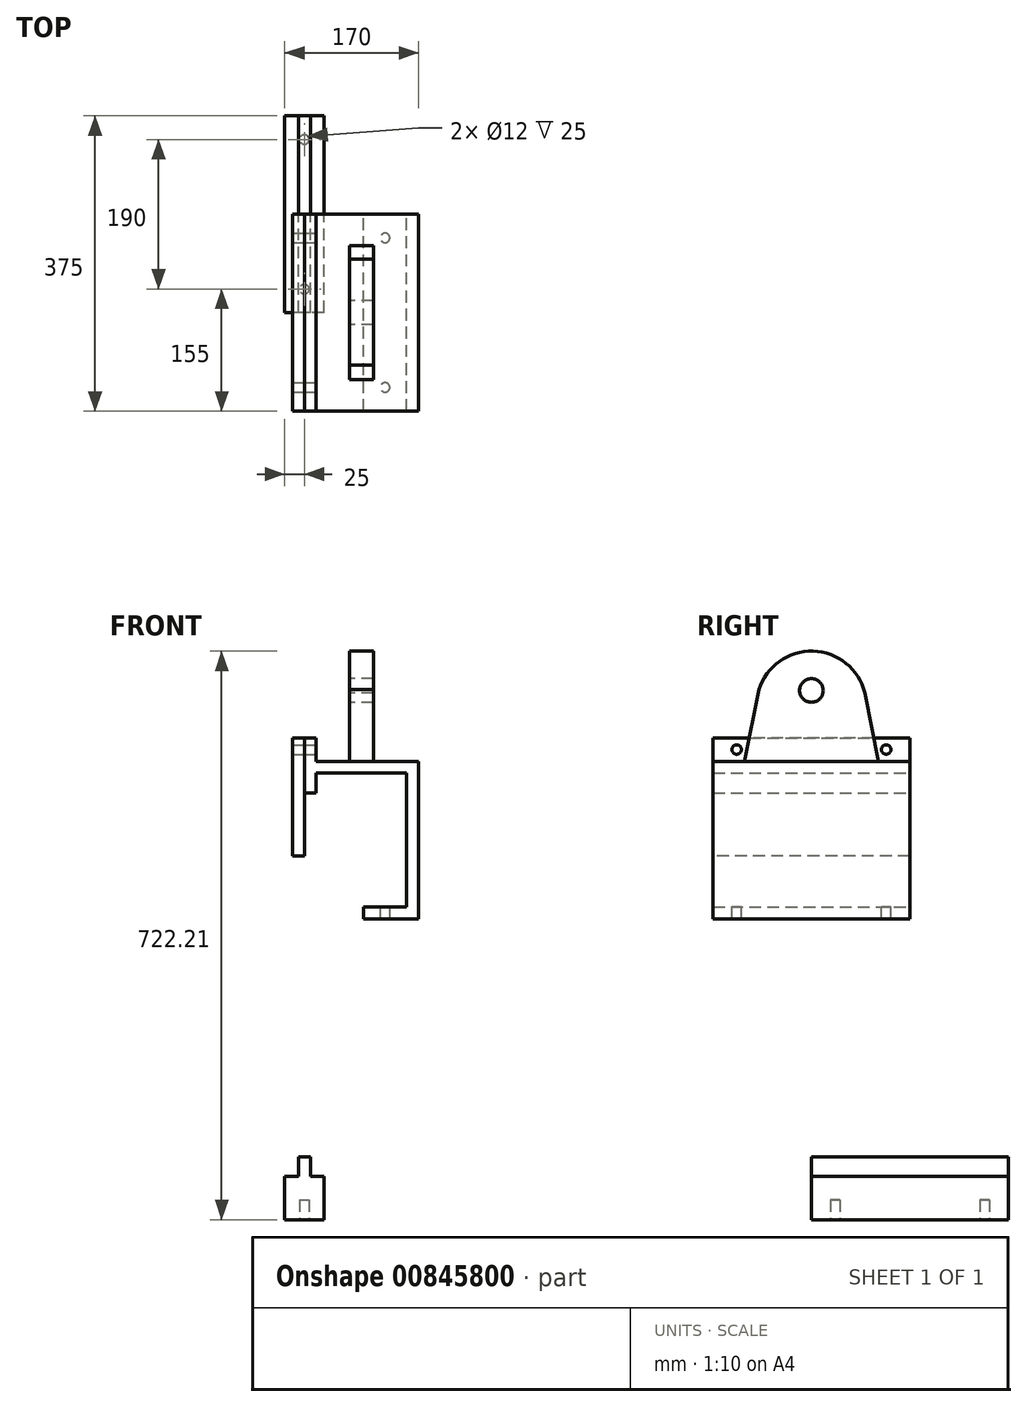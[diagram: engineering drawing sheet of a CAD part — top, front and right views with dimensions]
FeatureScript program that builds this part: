
annotation { "Feature Type Name" : "Feature", "Feature Type Description" : "" }
export const myFeature = defineFeature(function(context is Context, id is Id, definition is map)
    precondition{}
    {
        {
            var Q0;
            Q0=qCreatedBy(makeId("Front.planeOp"),FACE);
            var sketch = newSketch(context, id + "F0", { "sketchPlane" : qUnion([Q0])});
            skLineSegment(sketch, "E0", {"start": v(42.62, 18.6) * mm, "end": v(42.62, -96.4) * mm});
            skLineSegment(sketch, "E1", {"start": v(42.62, -96.4) * mm, "end": v(22.55, -96.4) * mm});
            skLineSegment(sketch, "E2", {"start": v(22.55, -96.4) * mm, "end": v(22.55, -88.4) * mm});
            skLineSegment(sketch, "E3", {"start": v(22.55, -88.4) * mm, "end": v(32.62, -88.4) * mm});
            skLineSegment(sketch, "E4", {"start": v(32.62, -88.4) * mm, "end": v(32.62, -31.1) * mm});
            skLineSegment(sketch, "E5", {"start": v(32.62, -31.1) * mm, "end": v(-23.38, -31.1) * mm});
            skLineSegment(sketch, "E6", {"start": v(-23.38, -31.1) * mm, "end": v(-23.38, -88.4) * mm});
            skLineSegment(sketch, "E7", {"start": v(-23.38, -88.4) * mm, "end": v(-4.88, -88.4) * mm});
            skLineSegment(sketch, "E8", {"start": v(-4.88, -88.4) * mm, "end": v(-4.88, -96.4) * mm});
            skLineSegment(sketch, "E9", {"start": v(-4.88, -96.4) * mm, "end": v(-30.88, -96.4) * mm});
            skLineSegment(sketch, "E10", {"start": v(-30.88, -96.4) * mm, "end": v(-30.88, -132.4) * mm});
            skLineSegment(sketch, "E11", {"start": v(-30.88, -132.4) * mm, "end": v(-34.88, -132.4) * mm});
            skLineSegment(sketch, "E12", {"start": v(-34.88, -132.4) * mm, "end": v(-34.88, -99.6) * mm});
            skLineSegment(sketch, "E13", {"start": v(-34.88, -99.6) * mm, "end": v(-65.38, -99.6) * mm});
            skLineSegment(sketch, "E14", {"start": v(-65.38, -99.6) * mm, "end": v(-65.38, -132.4) * mm});
            skLineSegment(sketch, "E15", {"start": v(-65.38, -132.4) * mm, "end": v(-70.38, -132.4) * mm});
            skLineSegment(sketch, "E16", {"start": v(-70.38, -132.4) * mm, "end": v(-70.38, 18.6) * mm});
            skPoint(sketch, "E17.end.orphan", {"position": v(-38.43, 18.6) * mm});
            skLineSegment(sketch, "E18", {"start": v(-70.38, 18.6) * mm, "end": v(42.62, 18.6) * mm});
            skLineSegment(sketch, "E19", {"start": v(0, 0) * mm, "end": v(242.06, 0) * mm});
            skLineSegment(sketch, "E20", {"start": v(242.06, -153.05) * mm, "end": v(242.06, 16.95) * mm});
            skLineSegment(sketch, "E21", {"start": v(242.06, 16.95) * mm, "end": v(342.06, 16.95) * mm});
            skLineSegment(sketch, "E22", {"start": v(342.06, 16.95) * mm, "end": v(342.06, -153.05) * mm});
            skLineSegment(sketch, "E23", {"start": v(342.06, -153.05) * mm, "end": v(242.06, -153.05) * mm});
            skLineSegment(sketch, "E24", {"start": v(75, 397.21) * mm, "end": v(130, 397.21) * mm});
            skLineSegment(sketch, "E25", {"start": v(130, 397.21) * mm, "end": v(130, 567.21) * mm});
            skLineSegment(sketch, "E26", {"start": v(130, 567.21) * mm, "end": v(15, 567.21) * mm});
            skLineSegment(sketch, "E27", {"start": v(15, 567.21) * mm, "end": v(15, 542.21) * mm});
            skLineSegment(sketch, "E28", {"start": v(75, 397.21) * mm, "end": v(75, 382.21) * mm});
            skLineSegment(sketch, "E29", {"start": v(75, 382.21) * mm, "end": v(145, 382.21) * mm});
            skLineSegment(sketch, "E30", {"start": v(145, 382.21) * mm, "end": v(145, 582.21) * mm});
            skLineSegment(sketch, "E31", {"start": v(145, 582.21) * mm, "end": v(0, 582.21) * mm});
            skLineSegment(sketch, "E32", {"start": v(0, 582.21) * mm, "end": v(0, 542.21) * mm});
            skLineSegment(sketch, "E33", {"start": v(0, 542.21) * mm, "end": v(15, 542.21) * mm});
            skSolve(sketch);
        }
        {
            var Q0;
            Q0=makeQuery(id+"F0.imprint","IMPRINT",FACE,{"disambiguationData":[TD([[makeQuery(id+"F0.imprint","IMPRINT",EDGE,{"derivedFrom":sQuery(id+"F0.wireOp",EDGE,"E24")}),-1.0]])]});
            extrude(context, id + "F1", {"entities" : qUnion([Q0]), "depth" : 250 * mm, "offsetDistance" : 25 * mm});
        }
        {
            var Q0;
            Q0=makeQuery(id+"F1.opExtrude","SWEPT_FACE",FACE,{"disambiguationData":[OSD([sQuery(id+"F0.wireOp",EDGE,"E24")])]});
            var sketch = newSketch(context, id + "F2", { "sketchPlane" : qUnion([Q0])});
            skCircle(sketch, "E34", {"center": v(102.5, -220) * mm, "radius": 6 * mm});
            skPoint(sketch, "E34.centerSnap0", {"position": v(102.5, -250) * mm});
            skCircle(sketch, "E35", {"center": v(102.5, -30) * mm, "radius": 6 * mm});
            skPoint(sketch, "E35.centerSnap0", {"position": v(102.5, 0) * mm});
            skLineSegment(sketch, "E36", {"start": v(102.5, 0) * mm, "end": v(102.5, -30) * mm});
            skLineSegment(sketch, "E37", {"start": v(102.5, -220) * mm, "end": v(102.5, -250) * mm});
            skSolve(sketch);
        }
        {
            var Q0;
            Q0 = qSketchRegion(id + "F2", true);
            extrude(context, id + "F3", {"entities" : qUnion([Q0]), "operationType" : NewBodyOperationType.REMOVE, "oppositeDirection" : true, "depth" : 15 * mm, "offsetDistance" : 25 * mm});
        }
        {
            var Q0;
            Q0=qCreatedBy(makeId("Top.planeOp"),FACE);
            var sketch = newSketch(context, id + "F4", { "sketchPlane" : qUnion([Q0])});
            skLineSegment(sketch, "E38.bottom", {"start": v(25, -125) * mm, "end": v(-25, -125) * mm});
            skLineSegment(sketch, "E38.top", {"start": v(25, 125) * mm, "end": v(-25, 125) * mm});
            skLineSegment(sketch, "E38.left", {"start": v(25, -125) * mm, "end": v(25, 125) * mm});
            skLineSegment(sketch, "E38.right", {"start": v(-25, -125) * mm, "end": v(-25, 125) * mm});
            skPoint(sketch, "E38.middle", {"position": v(0, 0) * mm});
            skSolve(sketch);
        }
        {
            var Q0;
            Q0 = qSketchRegion(id + "F4", true);
            extrude(context, id + "F5", {"entities" : qUnion([Q0]), "depth" : 55 * mm, "offsetDistance" : 25 * mm});
        }
        {
            var Q0;
            Q0=makeQuery(id+"F5.opExtrude","CAP_FACE",FACE,{"disambiguationData":[OSD([sQuery(id+"F4.wireOp",EDGE,"E38.bottom"),sQuery(id+"F4.wireOp",EDGE,"E38.top"),sQuery(id+"F4.wireOp",EDGE,"E38.left"),sQuery(id+"F4.wireOp",EDGE,"E38.right")])],"isStart":false});
            var sketch = newSketch(context, id + "F6", { "sketchPlane" : qUnion([Q0])});
            skLineSegment(sketch, "E39.bottom", {"start": v(7.5, -125) * mm, "end": v(-7.5, -125) * mm});
            skLineSegment(sketch, "E39.top", {"start": v(7.5, 125) * mm, "end": v(-7.5, 125) * mm});
            skLineSegment(sketch, "E39.left", {"start": v(7.5, -125) * mm, "end": v(7.5, 125) * mm});
            skLineSegment(sketch, "E39.right", {"start": v(-7.5, -125) * mm, "end": v(-7.5, 125) * mm});
            skPoint(sketch, "E39.middle", {"position": v(0, 0) * mm});
            skSolve(sketch);
        }
        {
            var Q0;
            Q0 = qSketchRegion(id + "F6", true);
            extrude(context, id + "F7", {"entities" : qUnion([Q0]), "operationType" : NewBodyOperationType.ADD, "depth" : 25 * mm, "offsetDistance" : 25 * mm});
        }
        {
            var Q0;
            Q0=makeQuery(id+"F5.opExtrude","CAP_FACE",FACE,{"disambiguationData":[OSD([sQuery(id+"F4.wireOp",EDGE,"E38.bottom"),sQuery(id+"F4.wireOp",EDGE,"E38.top"),sQuery(id+"F4.wireOp",EDGE,"E38.left"),sQuery(id+"F4.wireOp",EDGE,"E38.right")])],"isStart":true});
            var sketch = newSketch(context, id + "F8", { "sketchPlane" : qUnion([Q0])});
            skLineSegment(sketch, "E40", {"start": v(0, 125) * mm, "end": v(0, 95) * mm});
            skLineSegment(sketch, "E41", {"start": v(0, -125) * mm, "end": v(0, -95) * mm});
            skCircle(sketch, "E42", {"center": v(0, 95) * mm, "radius": 6 * mm});
            skCircle(sketch, "E43", {"center": v(0, -95) * mm, "radius": 6 * mm});
            skSolve(sketch);
        }
        {
            var Q0;
            Q0 = qSketchRegion(id + "F8", true);
            extrude(context, id + "F9", {"entities" : qUnion([Q0]), "operationType" : NewBodyOperationType.REMOVE, "oppositeDirection" : true, "depth" : 25 * mm, "offsetDistance" : 25 * mm});
        }
        {
            var Q0;
            Q0=makeQuery(id+"F1.opExtrude","SWEPT_FACE",FACE,{"disambiguationData":[OSD([sQuery(id+"F0.wireOp",EDGE,"E31")])]});
            var sketch = newSketch(context, id + "F10", { "sketchPlane" : qUnion([Q0])});
            skLineSegment(sketch, "E44.bottom", {"start": v(87.5, -210) * mm, "end": v(57.5, -210) * mm});
            skLineSegment(sketch, "E44.top", {"start": v(87.5, -40) * mm, "end": v(57.5, -40) * mm});
            skLineSegment(sketch, "E44.left", {"start": v(87.5, -210) * mm, "end": v(87.5, -40) * mm});
            skLineSegment(sketch, "E44.right", {"start": v(57.5, -210) * mm, "end": v(57.5, -40) * mm});
            skPoint(sketch, "E44.middle", {"position": v(72.5, -125) * mm});
            skPoint(sketch, "E44.middle.positionSnap0", {"position": v(72.5, 0) * mm});
            skPoint(sketch, "E44.middle.positionSnap1", {"position": v(0, -125) * mm});
            skPoint(sketch, "E44.centerSnap0", {"position": v(72.5, 0) * mm});
            skPoint(sketch, "E44.centerSnap1", {"position": v(0, -125) * mm});
            skSolve(sketch);
        }
        {
            var Q0;
            Q0 = qSketchRegion(id + "F10", true);
            extrude(context, id + "F11", {"entities" : qUnion([Q0]), "operationType" : NewBodyOperationType.ADD, "depth" : 140 * mm, "offsetDistance" : 25 * mm});
        }
        {
            var Q0;
            Q0=makeQuery(id+"F11.opExtrude","SWEPT_FACE",FACE,{"disambiguationData":[OSD([sQuery(id+"F10.wireOp",EDGE,"E44.right")])]});
            var sketch = newSketch(context, id + "F12", { "sketchPlane" : qUnion([Q0])});
            skCircle(sketch, "E45", {"center": v(125, 652.21) * mm, "radius": 70 * mm});
            skPoint(sketch, "E45.centerSnap0", {"position": v(40, 652.21) * mm});
            skPoint(sketch, "E45.centerSnap1", {"position": v(125, 722.21) * mm});
            skLineSegment(sketch, "E46", {"start": v(40, 582.21) * mm, "end": v(57.1, 669.23) * mm});
            skLineSegment(sketch, "E47", {"start": v(210, 582.21) * mm, "end": v(191.74, 673.32) * mm});
            skLineSegment(sketch, "E48", {"start": v(40, 582.21) * mm, "end": v(40, 722.21) * mm});
            skLineSegment(sketch, "E49", {"start": v(40, 722.21) * mm, "end": v(210, 722.21) * mm});
            skLineSegment(sketch, "E50", {"start": v(210, 722.21) * mm, "end": v(210, 585.68) * mm});
            skCircle(sketch, "E51", {"center": v(125, 672.25) * mm, "radius": 15 * mm});
            skSolve(sketch);
        }
        {
            var Q0;
            {var subQ0=sQuery(id+"F12.wireOp",EDGE,"E47");var subQ1=sQuery(id+"F12.wireOp",EDGE,"E45");var subQ2=makeQuery(id+"F12.imprint","INTERSECT",VERTEX,{"disambiguationData":[OD(0.0)],"derivedFrom":[subQ1,subQ0]});Q0=makeQuery(id+"F12.imprint","IMPRINT",FACE,{"disambiguationData":[TD([[makeQuery(id+"F12.imprint","IMPRINT",EDGE,{"disambiguationData":[TD([[subQ2,1.0]])],"derivedFrom":subQ1}),1.0]])]});}
            var Q1;
            {var subQ0=sQuery(id+"F12.wireOp",EDGE,"E46");var subQ1=sQuery(id+"F12.wireOp",EDGE,"E45");var subQ2=makeQuery(id+"F12.imprint","INTERSECT",VERTEX,{"disambiguationData":[OD(0.0)],"derivedFrom":[subQ1,subQ0]});Q1=makeQuery(id+"F12.imprint","IMPRINT",FACE,{"disambiguationData":[TD([[makeQuery(id+"F12.imprint","IMPRINT",EDGE,{"disambiguationData":[TD([[subQ2,-1.0]])],"derivedFrom":subQ1}),1.0]])]});}
            var Q2;
            {var subQ0=sQuery(id+"F12.wireOp",EDGE,"E48");Q2=makeQuery(id+"F12.imprint","IMPRINT",FACE,{"disambiguationData":[TD([[makeQuery(id+"F12.imprint","IMPRINT",EDGE,{"derivedFrom":subQ0}),1.0]])]});}
            var Q3;
            Q3=makeQuery(id+"F12.imprint","IMPRINT",FACE,{"disambiguationData":[TD([[makeQuery(id+"F12.imprint","IMPRINT",EDGE,{"derivedFrom":sQuery(id+"F12.wireOp",EDGE,"E51")}),1.0]])]});
            var Q4;
            {var subQ6=sQuery(id+"F12.wireOp",EDGE,"E50");Q4=makeQuery(id+"F12.imprint","IMPRINT",FACE,{"disambiguationData":[TD([[makeQuery(id+"F12.imprint","IMPRINT",EDGE,{"derivedFrom":subQ6}),-1.0]])]});}
            extrude(context, id + "F13", {"entities" : qUnion([Q0, Q1, Q2, Q3, Q4]), "operationType" : NewBodyOperationType.REMOVE, "oppositeDirection" : true, "depth" : 30 * mm, "offsetDistance" : 25 * mm});
        }
        {
            var Q0;
            Q0=makeQuery(id+"F1.opExtrude","SWEPT_FACE",FACE,{"disambiguationData":[OSD([sQuery(id+"F0.wireOp",EDGE,"E31")])]});
            var sketch = newSketch(context, id + "F14", { "sketchPlane" : qUnion([Q0])});
            skLineSegment(sketch, "E52.bottom", {"start": v(0, 0) * mm, "end": v(15, 0) * mm});
            skLineSegment(sketch, "E52.top", {"start": v(0, -250) * mm, "end": v(15, -250) * mm});
            skLineSegment(sketch, "E52.left", {"start": v(0, 0) * mm, "end": v(0, -250) * mm});
            skLineSegment(sketch, "E52.right", {"start": v(15, 0) * mm, "end": v(15, -250) * mm});
            skSolve(sketch);
        }
        {
            var Q0;
            Q0 = qSketchRegion(id + "F14", true);
            extrude(context, id + "F15", {"entities" : qUnion([Q0]), "operationType" : NewBodyOperationType.ADD, "depth" : 30 * mm, "offsetDistance" : 25 * mm});
        }
        {
            var Q0;
            Q0=makeQuery(id+"F15.opExtrude","SWEPT_FACE",FACE,{"disambiguationData":[OSD([sQuery(id+"F14.wireOp",EDGE,"E52.right")])]});
            var sketch = newSketch(context, id + "F16", { "sketchPlane" : qUnion([Q0])});
            skCircle(sketch, "E53", {"center": v(-220, 597.21) * mm, "radius": 6 * mm});
            skPoint(sketch, "E53.centerSnap0", {"position": v(-250, 597.21) * mm});
            skCircle(sketch, "E54", {"center": v(-30, 597.21) * mm, "radius": 6 * mm});
            skPoint(sketch, "E54.centerSnap0", {"position": v(0, 597.21) * mm});
            skSolve(sketch);
        }
        {
            var Q0;
            Q0 = qSketchRegion(id + "F16", true);
            extrude(context, id + "F17", {"entities" : qUnion([Q0]), "operationType" : NewBodyOperationType.REMOVE, "oppositeDirection" : true, "depth" : 15 * mm, "offsetDistance" : 25 * mm});
        }
        {
            var Q0;
            Q0=makeQuery(id+"F15.boolean.opBoolean","MERGE",FACE,{"derivedFrom":[makeQuery(id+"F1.opExtrude","SWEPT_FACE",FACE,{"disambiguationData":[OSD([sQuery(id+"F0.wireOp",EDGE,"E32")])]}),makeQuery(id+"F15.opExtrude","SWEPT_FACE",FACE,{"disambiguationData":[OSD([sQuery(id+"F14.wireOp",EDGE,"E52.left")])]})]});
            var sketch = newSketch(context, id + "F18", { "sketchPlane" : qUnion([Q0])});
            skLineSegment(sketch, "E55.bottom", {"start": v(0, 612.21) * mm, "end": v(250, 612.21) * mm});
            skLineSegment(sketch, "E55.top", {"start": v(0, 462.21) * mm, "end": v(250, 462.21) * mm});
            skLineSegment(sketch, "E55.left", {"start": v(0, 612.21) * mm, "end": v(0, 462.21) * mm});
            skLineSegment(sketch, "E55.right", {"start": v(250, 612.21) * mm, "end": v(250, 462.21) * mm});
            skCircle(sketch, "E56", {"center": v(30, 597.21) * mm, "radius": 6 * mm});
            skCircle(sketch, "E57", {"center": v(220, 597.21) * mm, "radius": 6 * mm});
            skSolve(sketch);
        }
        {
            var Q0;
            Q0 = qSketchRegion(id + "F18", true);
            extrude(context, id + "F19", {"entities" : qUnion([Q0]), "depth" : 15 * mm, "offsetDistance" : 25 * mm});
        }
    });
